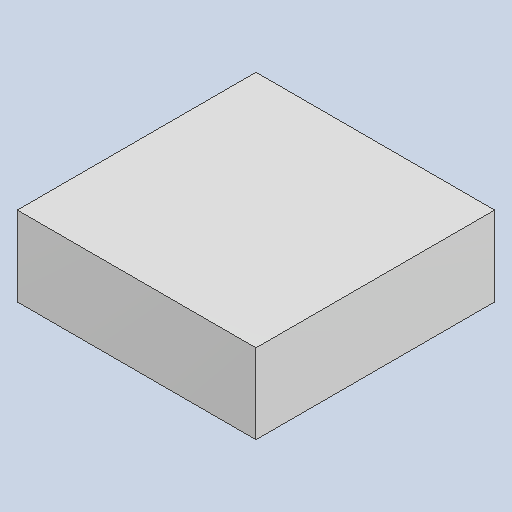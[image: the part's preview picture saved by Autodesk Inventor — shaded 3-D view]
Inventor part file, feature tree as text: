
AUTODESK INVENTOR PART (.ipt)
format: ipt  version: 2023.4 (Build 274418000, 418)  size: 79,872 bytes
history: native  units: mm
features: extrude x1
ambient origin geometry x8: Origin, YZ Plane, XZ Plane, XY Plane, X Axis, Y Axis, Z Axis, Center Point
bodies: Solid1 (feature_tree)
feature tree (1):
  extrude  "Extruded_16"  [1 undecoded]
note: 1 required parameter value undecoded (feature->parameter linkage not recoverable at this tier; creation-order binding heuristic only, values carry confidence <= 0.55)
